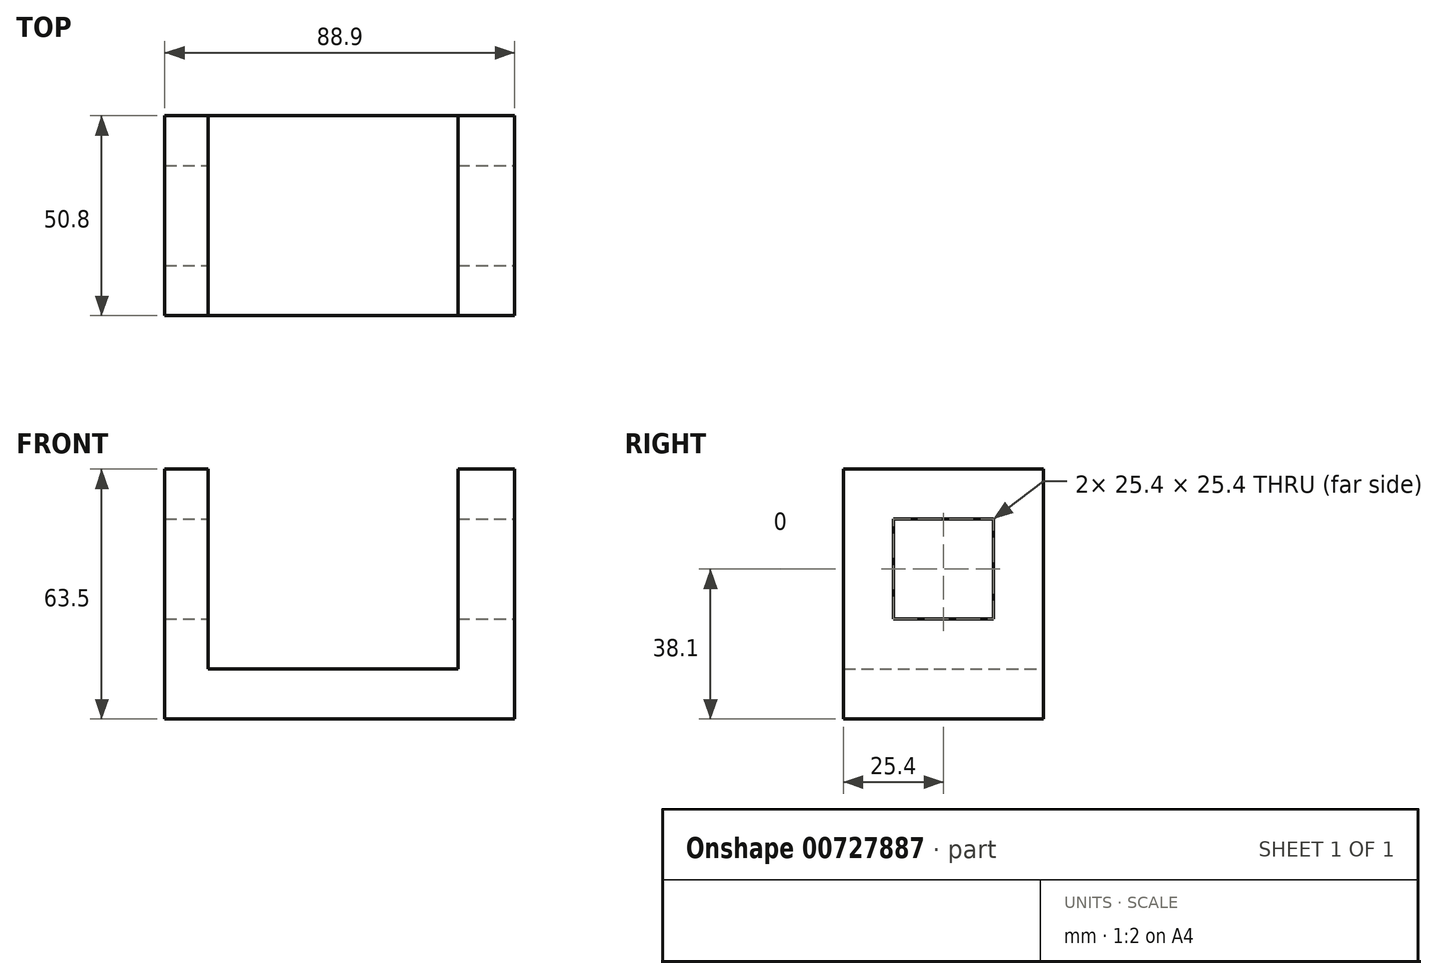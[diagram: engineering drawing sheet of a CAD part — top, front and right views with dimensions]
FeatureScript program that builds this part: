
annotation { "Feature Type Name" : "Feature", "Feature Type Description" : "" }
export const myFeature = defineFeature(function(context is Context, id is Id, definition is map)
    precondition{}
    {
        {
            var Q0;
            Q0=qCreatedBy(makeId("Front.planeOp"),FACE);
            var sketch = newSketch(context, id + "F0", { "sketchPlane" : qUnion([Q0])});
            skLineSegment(sketch, "E0.bottom", {"start": v(46.2, -31.75) * mm, "end": v(-42.7, -31.75) * mm});
            skLineSegment(sketch, "E0.top", {"start": v(46.2, 31.75) * mm, "end": v(-42.7, 31.75) * mm});
            skLineSegment(sketch, "E0.left", {"start": v(46.2, -31.75) * mm, "end": v(46.2, 31.75) * mm});
            skLineSegment(sketch, "E0.right", {"start": v(-42.7, -31.75) * mm, "end": v(-42.7, 31.75) * mm});
            skPoint(sketch, "E0.middle", {"position": v(1.74, 0) * mm});
            skLineSegment(sketch, "E1.bottom", {"start": v(-31.75, 31.75) * mm, "end": v(31.75, 31.75) * mm});
            skLineSegment(sketch, "E1.top", {"start": v(-31.75, -19.05) * mm, "end": v(31.75, -19.05) * mm});
            skLineSegment(sketch, "E1.left", {"start": v(-31.75, 31.75) * mm, "end": v(-31.75, -19.05) * mm});
            skLineSegment(sketch, "E1.right", {"start": v(31.75, 31.75) * mm, "end": v(31.75, -19.05) * mm});
            skSolve(sketch);
        }
        {
            var Q0;
            Q0=makeQuery(id+"F0.imprint","IMPRINT",FACE,{"disambiguationData":[TD([[makeQuery(id+"F0.imprint","IMPRINT",EDGE,{"derivedFrom":sQuery(id+"F0.wireOp",EDGE,"E0.bottom")}),-1.0]])]});
            extrude(context, id + "F1", {"entities" : qUnion([Q0]), "depth" : 50.8 * mm, "offsetDistance" : 25.4 * mm});
        }
        {
            var Q0;
            Q0=makeQuery(id+"F1.opExtrude","SWEPT_FACE",FACE,{"disambiguationData":[OSD([sQuery(id+"F0.wireOp",EDGE,"E0.left")])]});
            var sketch = newSketch(context, id + "F2", { "sketchPlane" : qUnion([Q0])});
            skLineSegment(sketch, "E2.bottom", {"start": v(-38.1, 19.05) * mm, "end": v(-12.7, 19.05) * mm});
            skLineSegment(sketch, "E2.top", {"start": v(-38.1, -6.35) * mm, "end": v(-12.7, -6.35) * mm});
            skLineSegment(sketch, "E2.left", {"start": v(-38.1, 19.05) * mm, "end": v(-38.1, -6.35) * mm});
            skLineSegment(sketch, "E2.right", {"start": v(-12.7, 19.05) * mm, "end": v(-12.7, -6.35) * mm});
            skSolve(sketch);
        }
        {
            var Q0;
            Q0=makeQuery(id+"F2.imprint","IMPRINT",FACE,{"disambiguationData":[TD([[makeQuery(id+"F2.imprint","IMPRINT",EDGE,{"derivedFrom":sQuery(id+"F2.wireOp",EDGE,"E2.bottom")}),-1.0]])]});
            extrude(context, id + "F3", {"entities" : qUnion([Q0]), "operationType" : NewBodyOperationType.REMOVE, "oppositeDirection" : true, "depth" : 88.9 * mm, "offsetDistance" : 25.4 * mm});
        }
    });
